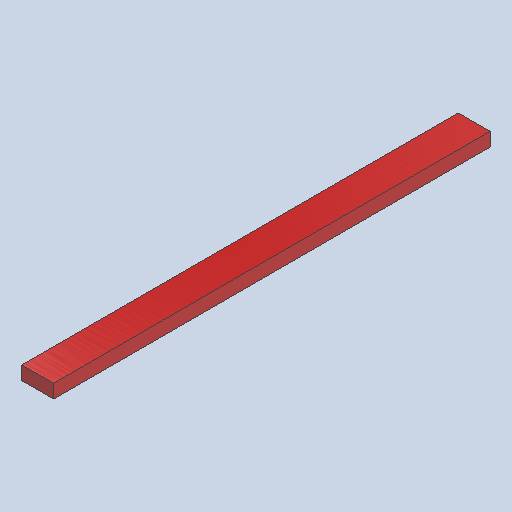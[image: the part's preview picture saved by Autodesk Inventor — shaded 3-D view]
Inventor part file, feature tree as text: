
AUTODESK INVENTOR PART (.ipt)
format: ipt  version: 2025 (Build 290162000, 162)  size: 96,256 bytes
history: native  units: in
note: dims shown in document units (in); Inventor stores cm internally (conversion verified against a paired STEP export)
features: other x4, sketch x1
ambient origin geometry x8: Origin, YZ Plane, XZ Plane, XY Plane, X Axis, Y Axis, Z Axis, Center Point
bodies: Solid1 (feature_tree)
feature tree (5):
  other  "4x2x4.ipt"
  other  "Solid1::4x2x4.ipt"
  other  "TaggingFeature1"
  sketch  "Sketch1"  dims[d0=0.3937in]
  other  "Finish1"
